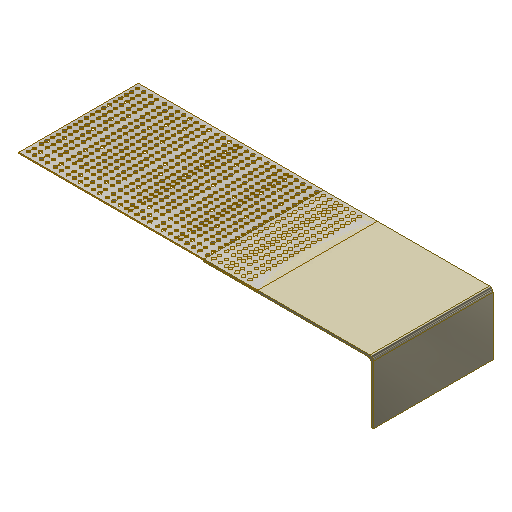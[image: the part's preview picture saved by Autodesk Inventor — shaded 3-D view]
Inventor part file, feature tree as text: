
AUTODESK INVENTOR PART (.ipt)
format: ipt  version: 2025 (Build 290162000, 162)  size: 2,790,400 bytes
history: native  units: mm
features: extrude x3, sketch x3, other x2, fillet x2
ambient origin geometry x8: Origin, YZ Plane, XZ Plane, XY Plane, X Axis, Y Axis, Z Axis, Center Point
bodies: Body1 (feature_tree), Body2 (feature_tree)
feature tree (10):
  other  "Sólido1"
  extrude  "Extrusão1"  Depth=14.0mm
  fillet  "Arredondamento1"  Radius=0.2mm
  fillet  "Arredondamento2"  Radius=5.2mm
  extrude  "Extrusão2"  Depth=10.0mm TaperAngle=0.0deg
  extrude  "Extrusão3"  Depth=0.3mm
  sketch  "Esboço1"  dims[d0=5.0mm d1=14.0mm d2=0.2mm d3=5.2mm]
  sketch  "Esboço2"  dims[d4=0.2mm d5=10.0mm d6=0.0mm]
  other  "Sólido2"
  sketch  "Esboço3"  dims[d7=0.3mm d8=0.3mm d9=20.0mm d10=10.0mm d11=0.1mm d12=0.0mm d13=0.1mm d14=0.0mm]
